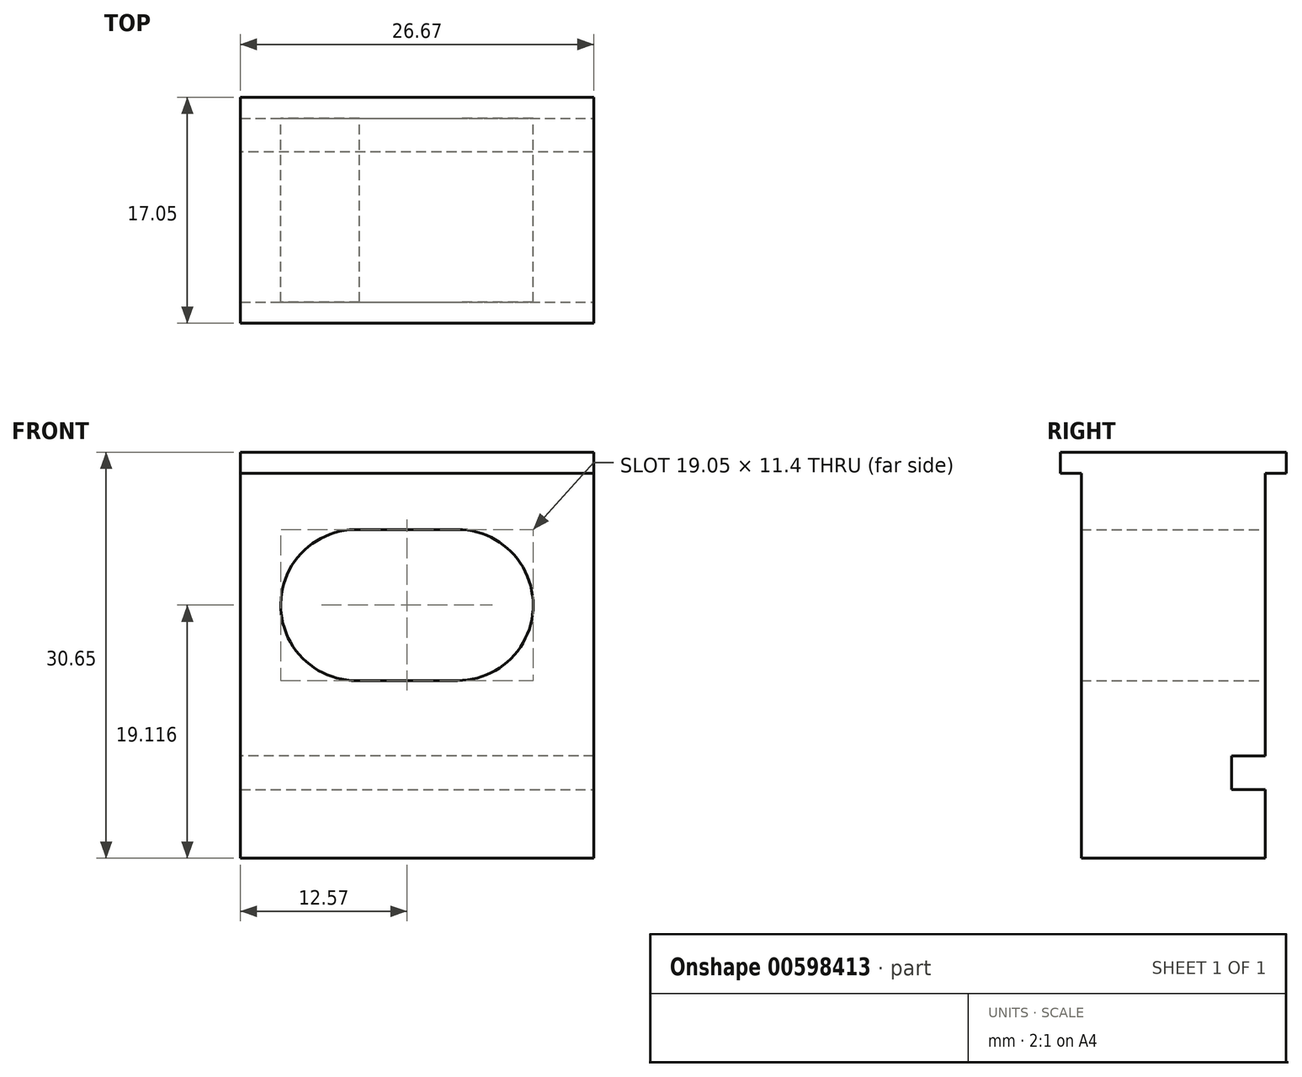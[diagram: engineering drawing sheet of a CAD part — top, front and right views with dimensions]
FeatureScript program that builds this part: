
annotation { "Feature Type Name" : "Feature", "Feature Type Description" : "" }
export const myFeature = defineFeature(function(context is Context, id is Id, definition is map)
    precondition{}
    {
        {
            var Q0;
            Q0=qCreatedBy(makeId("Front.planeOp"),FACE);
            var sketch = newSketch(context, id + "F0", { "sketchPlane" : qUnion([Q0])});
            skLineSegment(sketch, "E0.bottom", {"start": v(-12.7, 12.7) * mm, "end": v(12.7, 12.7) * mm});
            skLineSegment(sketch, "E0.top", {"start": v(-12.7, -12.7) * mm, "end": v(12.7, -12.7) * mm});
            skLineSegment(sketch, "E0.left", {"start": v(-12.7, 12.7) * mm, "end": v(-12.7, -12.7) * mm});
            skLineSegment(sketch, "E0.right", {"start": v(12.7, 12.7) * mm, "end": v(12.7, -12.7) * mm});
            skPoint(sketch, "E0.middle", {"position": v(0, 0) * mm});
            skLineSegment(sketch, "E1", {"start": v(-12.7, -11.18) * mm, "end": v(12.7, -11.18) * mm});
            skLineSegment(sketch, "E2", {"start": v(12.7, -11.18) * mm, "end": v(12.7, -8.64) * mm});
            skLineSegment(sketch, "E3", {"start": v(12.7, -8.64) * mm, "end": v(-12.7, -8.64) * mm});
            skLineSegment(sketch, "E4", {"start": v(-12.7, -8.64) * mm, "end": v(-12.7, -4.1) * mm});
            skPoint(sketch, "E5", {"position": v(0, 2.76) * mm});
            skArc(sketch, "E6", {"start": v(-3.58, 8.45) * mm, "mid": v(-9.52, 2.86) * mm, "end": v(-3.8, -2.95) * mm});
            skArc(sketch, "E7", {"start": v(3.82, -2.95) * mm, "mid": v(9.52, 2.76) * mm, "end": v(3.82, 8.46) * mm});
            skLineSegment(sketch, "E8", {"start": v(-4.07, 8.45) * mm, "end": v(3.82, 8.46) * mm});
            skLineSegment(sketch, "E9", {"start": v(-3.85, -2.95) * mm, "end": v(3.82, -2.95) * mm});
            skSolve(sketch);
        }
        {
            var Q0;
            {var subQ8=sQuery(id+"F0.wireOp",EDGE,"E0.bottom");Q0=makeQuery(id+"F0.imprint","IMPRINT",FACE,{"disambiguationData":[TD([[makeQuery(id+"F0.imprint","IMPRINT",EDGE,{"derivedFrom":subQ8}),-1.0]])]});}
            var Q1;
            {var subQ0=sQuery(id+"F0.wireOp",EDGE,"E1");Q1=makeQuery(id+"F0.imprint","IMPRINT",FACE,{"disambiguationData":[TD([[makeQuery(id+"F0.imprint","IMPRINT",EDGE,{"derivedFrom":subQ0}),1.0]])]});}
            var Q2;
            {var subQ0=sQuery(id+"F0.wireOp",EDGE,"E0.top");Q2=makeQuery(id+"F0.imprint","IMPRINT",FACE,{"disambiguationData":[TD([[makeQuery(id+"F0.imprint","IMPRINT",EDGE,{"derivedFrom":subQ0}),1.0]])]});}
            extrude(context, id + "F1", {"entities" : qUnion([Q0, Q1, Q2]), "depth" : 13.87 * mm, "offsetDistance" : 25.4 * mm});
        }
        {
            var Q0;
            {var subQ0=sQuery(id+"F0.wireOp",EDGE,"E1");Q0=makeQuery(id+"F0.imprint","IMPRINT",FACE,{"disambiguationData":[TD([[makeQuery(id+"F0.imprint","IMPRINT",EDGE,{"derivedFrom":subQ0}),1.0]])]});}
            extrude(context, id + "F2", {"entities" : qUnion([Q0]), "operationType" : NewBodyOperationType.REMOVE, "depth" : 2.54 * mm, "offsetDistance" : 25.4 * mm});
        }
        {
            var Q0;
            Q0=makeQuery(id+"F1.opExtrude","SWEPT_FACE",FACE,{"disambiguationData":[OSD([sQuery(id+"F0.wireOp",EDGE,"E0.right"),sQuery(id+"F0.wireOp",EDGE,"E2")])]});
            extrude(context, id + "F3", {"entities" : qUnion([Q0]), "operationType" : NewBodyOperationType.ADD, "depth" : 1.4 * mm, "offsetDistance" : 25.4 * mm});
        }
        {
            var Q0;
            Q0=makeQuery(id+"F1.opExtrude","SWEPT_FACE",FACE,{"disambiguationData":[OSD([sQuery(id+"F0.wireOp",EDGE,"E0.left"),sQuery(id+"F0.wireOp",EDGE,"E4")])]});
            extrude(context, id + "F4", {"entities" : qUnion([Q0]), "operationType" : NewBodyOperationType.REMOVE, "oppositeDirection" : true, "depth" : 0.13 * mm, "offsetDistance" : 25.4 * mm});
        }
        {
            var Q0;
            {var subQ0=sQuery(id+"F0.wireOp",EDGE,"E0.top");Q0=makeQuery(id+"F3.boolean.opBoolean","MERGE",FACE,{"derivedFrom":[makeQuery(id+"F1.opExtrude","SWEPT_FACE",FACE,{"disambiguationData":[OSD([subQ0])]}),makeQuery(id+"F3.opExtrude","SWEPT_FACE",FACE,{"disambiguationData":[OSD([subQ0,sQuery(id+"F0.wireOp",EDGE,"E0.right")])]})]});}
            extrude(context, id + "F5", {"entities" : qUnion([Q0]), "operationType" : NewBodyOperationType.ADD, "depth" : 3.66 * mm, "offsetDistance" : 25.4 * mm});
        }
        {
            var Q0;
            {var subQ0=sQuery(id+"F0.wireOp",EDGE,"E0.bottom");Q0=makeQuery(id+"F3.boolean.opBoolean","MERGE",FACE,{"derivedFrom":[makeQuery(id+"F1.opExtrude","SWEPT_FACE",FACE,{"disambiguationData":[OSD([subQ0])]}),makeQuery(id+"F3.opExtrude","SWEPT_FACE",FACE,{"disambiguationData":[OSD([subQ0,sQuery(id+"F0.wireOp",EDGE,"E0.right")])]})]});}
            var sketch = newSketch(context, id + "F6", { "sketchPlane" : qUnion([Q0])});
            skLineSegment(sketch, "E10", {"start": v(0.13, 0) * mm, "end": v(0.13, -13.87) * mm});
            skSolve(sketch);
        }
        {
            var Q0;
            {var subQ0=sQuery(id+"F6.wireOp",EDGE,"E10");Q0=makeQuery(id+"F6.imprint","IMPRINT",FACE,{"disambiguationData":[TD([[makeQuery(id+"F6.imprint","IMPRINT",EDGE,{"derivedFrom":subQ0}),1.0]])]});}
            extrude(context, id + "F7", {"entities" : qUnion([Q0]), "operationType" : NewBodyOperationType.ADD, "depth" : 1.59 * mm, "offsetDistance" : 25.4 * mm});
        }
        {
            var Q0;
            {var subQ0=sQuery(id+"F0.wireOp",EDGE,"E0.right");var subQ1=sQuery(id+"F0.wireOp",EDGE,"E0.bottom");var subQ2=makeQuery(id+"F3.boolean.opBoolean","MERGE",EDGE,{"derivedFrom":[makeQuery(id+"F1.opExtrude","CAP_EDGE",EDGE,{"disambiguationData":[OSD([subQ1])],"isStart":false}),makeQuery(id+"F3.opExtrude","SWEPT_EDGE",EDGE,{"disambiguationData":[OSD([subQ1,subQ0]),TDD([makeQuery(id+"F1.opExtrude","CAP_VERTEX",VERTEX,{"disambiguationData":[OSD([subQ1,subQ0])],"isStart":false})])]})]});var subQ3=sQuery(id+"F0.wireOp",EDGE,"E0.top");var subQ4=sQuery(id+"F0.wireOp",EDGE,"E2");Q0=makeQuery(id+"F7.boolean.opBoolean","MERGE",FACE,{"derivedFrom":[makeQuery(id+"F5.boolean.opBoolean","MERGE",FACE,{"derivedFrom":[makeQuery(id+"F3.boolean.opBoolean","MERGE",FACE,{"derivedFrom":[makeQuery(id+"F1.opExtrude","CAP_FACE",FACE,{"disambiguationData":[OSD([subQ1,subQ3,sQuery(id+"F0.wireOp",EDGE,"E0.left"),subQ0,subQ4,sQuery(id+"F0.wireOp",EDGE,"E4"),sQuery(id+"F0.wireOp",EDGE,"E6"),sQuery(id+"F0.wireOp",EDGE,"E7"),sQuery(id+"F0.wireOp",EDGE,"E8"),sQuery(id+"F0.wireOp",EDGE,"E9")])],"isStart":false}),makeQuery(id+"F3.opExtrude","SWEPT_FACE",FACE,{"disambiguationData":[OSD([subQ0,subQ4]),TDD([makeQuery(id+"F1.opExtrude","CAP_EDGE",EDGE,{"disambiguationData":[OSD([subQ0,subQ4])],"isStart":false})])]})]}),makeQuery(id+"F5.opExtrude","SWEPT_FACE",FACE,{"disambiguationData":[OSD([subQ3,subQ0]),TDD([makeQuery(id+"F3.boolean.opBoolean","MERGE",EDGE,{"derivedFrom":[makeQuery(id+"F1.opExtrude","CAP_EDGE",EDGE,{"disambiguationData":[OSD([subQ3])],"isStart":false}),makeQuery(id+"F3.opExtrude","SWEPT_EDGE",EDGE,{"disambiguationData":[OSD([subQ3,subQ0]),TDD([makeQuery(id+"F1.opExtrude","CAP_VERTEX",VERTEX,{"disambiguationData":[OSD([subQ3,subQ0])],"isStart":false})])]})]})])]})]}),makeQuery(id+"F7.opExtrude","SWEPT_FACE",FACE,{"disambiguationData":[OSD([subQ1,subQ0]),TDD([makeQuery(id+"F6.imprint","IMPRINT",EDGE,{"disambiguationData":[TD([[makeQuery(id+"F6.imprint","INTERSECT",VERTEX,{"derivedFrom":[subQ2,sQuery(id+"F6.wireOp",EDGE,"E10")]}),-1.0]])],"derivedFrom":subQ2})])]})]});}
            var sketch = newSketch(context, id + "F8", { "sketchPlane" : qUnion([Q0])});
            skLineSegment(sketch, "E11", {"start": v(0.13, 12.7) * mm, "end": v(14.1, 12.7) * mm});
            skSolve(sketch);
        }
        {
            var Q0;
            {var subQ0=sQuery(id+"F8.wireOp",EDGE,"E11");Q0=makeQuery(id+"F8.imprint","IMPRINT",FACE,{"disambiguationData":[TD([[makeQuery(id+"F8.imprint","IMPRINT",EDGE,{"derivedFrom":subQ0}),1.0]])]});}
            extrude(context, id + "F9", {"entities" : qUnion([Q0]), "operationType" : NewBodyOperationType.ADD, "depth" : 1.59 * mm, "offsetDistance" : 25.4 * mm});
        }
        {
            var Q0;
            {var subQ0=sQuery(id+"F0.wireOp",EDGE,"E0.right");var subQ1=sQuery(id+"F0.wireOp",EDGE,"E0.bottom");var subQ2=makeQuery(id+"F3.boolean.opBoolean","MERGE",EDGE,{"derivedFrom":[makeQuery(id+"F1.opExtrude","CAP_EDGE",EDGE,{"disambiguationData":[OSD([subQ1])],"isStart":true}),makeQuery(id+"F3.opExtrude","SWEPT_EDGE",EDGE,{"disambiguationData":[OSD([subQ1,subQ0]),TDD([makeQuery(id+"F1.opExtrude","CAP_VERTEX",VERTEX,{"disambiguationData":[OSD([subQ1,subQ0])],"isStart":true})])]})]});var subQ3=makeQuery(id+"F1.opExtrude","SWEPT_FACE",FACE,{"disambiguationData":[OSD([subQ1])]});var subQ4=sQuery(id+"F0.wireOp",EDGE,"E2");var subQ6=sQuery(id+"F0.wireOp",EDGE,"E9");var subQ7=sQuery(id+"F0.wireOp",EDGE,"E8");var subQ8=sQuery(id+"F0.wireOp",EDGE,"E7");var subQ9=sQuery(id+"F0.wireOp",EDGE,"E6");var subQ10=sQuery(id+"F0.wireOp",EDGE,"E4");var subQ11=sQuery(id+"F0.wireOp",EDGE,"E0.left");var subQ12=makeQuery(id+"F1.opExtrude","CAP_FACE",FACE,{"disambiguationData":[OSD([subQ1,sQuery(id+"F0.wireOp",EDGE,"E0.top"),subQ11,subQ0,subQ4,subQ10,subQ9,subQ8,subQ7,subQ6])],"isStart":true});Q0=makeQuery(id+"F7.boolean.opBoolean","MERGE",FACE,{"derivedFrom":[makeQuery(id+"F3.boolean.opBoolean","MERGE",FACE,{"derivedFrom":[makeQuery(id+"F2.boolean.opBoolean","SPLIT",FACE,{"disambiguationData":[TD([subQ3])],"derivedFrom":subQ12}),makeQuery(id+"F3.opExtrude","SWEPT_FACE",FACE,{"disambiguationData":[OSD([subQ0,subQ4]),TDD([makeQuery(id+"F2.boolean.opBoolean","SPLIT",EDGE,{"disambiguationData":[TD([subQ3])],"derivedFrom":makeQuery(id+"F1.opExtrude","CAP_EDGE",EDGE,{"disambiguationData":[OSD([subQ0,subQ4])],"isStart":true})})])]})]}),makeQuery(id+"F7.opExtrude","SWEPT_FACE",FACE,{"disambiguationData":[OSD([subQ1,subQ0]),TDD([makeQuery(id+"F6.imprint","IMPRINT",EDGE,{"disambiguationData":[TD([[makeQuery(id+"F6.imprint","INTERSECT",VERTEX,{"derivedFrom":[subQ2,sQuery(id+"F6.wireOp",EDGE,"E10")]}),-1.0]])],"derivedFrom":subQ2})])]})]});}
            var sketch = newSketch(context, id + "F10", { "sketchPlane" : qUnion([Q0])});
            skLineSegment(sketch, "E12", {"start": v(-0.13, 12.7) * mm, "end": v(-14.1, 12.7) * mm});
            skSolve(sketch);
        }
        {
            var Q0;
            {var subQ0=sQuery(id+"F10.wireOp",EDGE,"E12");Q0=makeQuery(id+"F10.imprint","IMPRINT",FACE,{"disambiguationData":[TD([[makeQuery(id+"F10.imprint","IMPRINT",EDGE,{"derivedFrom":subQ0}),-1.0]])]});}
            extrude(context, id + "F11", {"entities" : qUnion([Q0]), "operationType" : NewBodyOperationType.ADD, "depth" : 1.59 * mm, "offsetDistance" : 25.4 * mm});
        }
        {
            var Q0;
            {var subQ0=sQuery(id+"F6.wireOp",EDGE,"E10");var subQ1=sQuery(id+"F0.wireOp",EDGE,"E0.right");var subQ2=sQuery(id+"F0.wireOp",EDGE,"E0.bottom");Q0=makeQuery(id+"F11.boolean.opBoolean","MERGE",FACE,{"derivedFrom":[makeQuery(id+"F9.boolean.opBoolean","MERGE",FACE,{"derivedFrom":[makeQuery(id+"F7.opExtrude","SWEPT_FACE",FACE,{"disambiguationData":[OSD([subQ0])]}),makeQuery(id+"F9.opExtrude","SWEPT_FACE",FACE,{"disambiguationData":[OSD([subQ2,subQ1,subQ0])]})]}),makeQuery(id+"F11.opExtrude","SWEPT_FACE",FACE,{"disambiguationData":[OSD([subQ2,subQ1,subQ0])]})]});}
            var Q1;
            {var subQ0=sQuery(id+"F0.wireOp",EDGE,"E0.left");Q1=makeQuery(id+"F5.boolean.opBoolean","MERGE",FACE,{"derivedFrom":[makeQuery(id+"F4.boolean.opBoolean","COPY",FACE,{"derivedFrom":makeQuery(id+"F4.opExtrude","CAP_FACE",FACE,{"disambiguationData":[OSD([subQ0,sQuery(id+"F0.wireOp",EDGE,"E4")])],"isStart":false})}),makeQuery(id+"F5.opExtrude","SWEPT_FACE",FACE,{"disambiguationData":[OSD([sQuery(id+"F0.wireOp",EDGE,"E0.top"),subQ0])]})]});}
            extrude(context, id + "F12", {"entities" : qUnion([Q0]), "operationType" : NewBodyOperationType.ADD, "endBound" : BoundingType.UP_TO_SURFACE, "depth" : 25.4 * mm, "endBoundEntityFace" : qUnion([Q1]), "offsetDistance" : 25.4 * mm});
        }
    });
